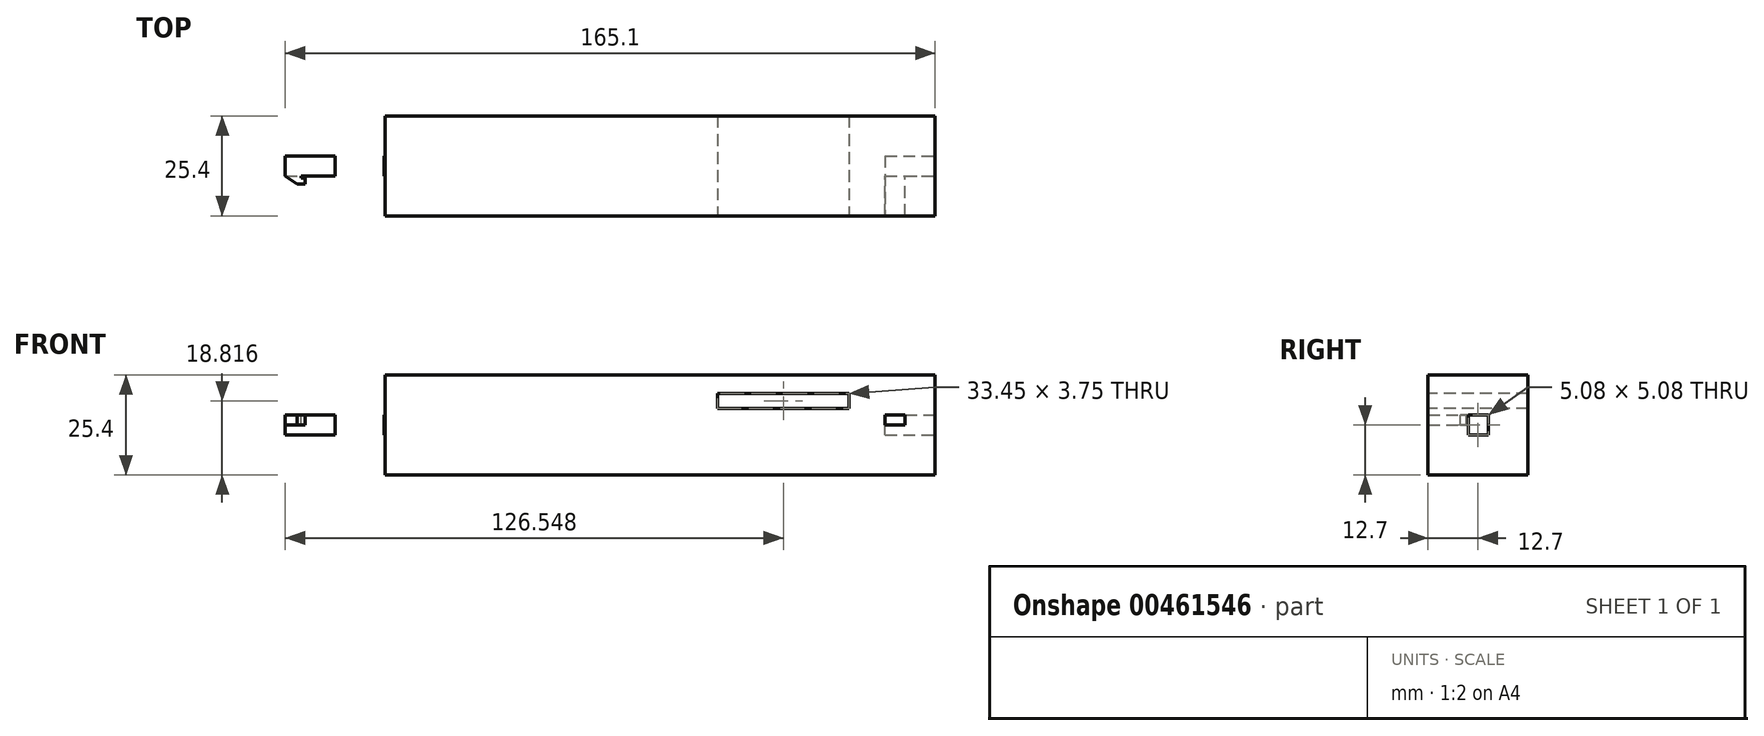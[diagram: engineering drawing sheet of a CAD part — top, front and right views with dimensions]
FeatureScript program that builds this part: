
annotation { "Feature Type Name" : "Feature", "Feature Type Description" : "" }
export const myFeature = defineFeature(function(context is Context, id is Id, definition is map)
    precondition{}
    {
        {
            var Q0;
            Q0=qCreatedBy(makeId("Top.planeOp"),FACE);
            var sketch = newSketch(context, id + "F0", { "sketchPlane" : qUnion([Q0])});
            skLineSegment(sketch, "E0.bottom", {"start": v(76.2, -12.7) * mm, "end": v(-76.2, -12.7) * mm});
            skLineSegment(sketch, "E0.top", {"start": v(76.2, 12.7) * mm, "end": v(-76.2, 12.7) * mm});
            skLineSegment(sketch, "E0.left", {"start": v(76.2, -12.7) * mm, "end": v(76.2, 12.7) * mm});
            skLineSegment(sketch, "E0.right", {"start": v(-76.2, -12.7) * mm, "end": v(-76.2, 12.7) * mm});
            skPoint(sketch, "E0.middle", {"position": v(0, 0) * mm});
            skSolve(sketch);
        }
        {
            var Q0;
            Q0 = qSketchRegion(id + "F0", true);
            var Q1;
            Q1=makeQuery(id+"F0.imprint","IMPRINT",FACE,{"disambiguationData":[TD([[makeQuery(id+"F0.imprint","IMPRINT",EDGE,{"derivedFrom":sQuery(id+"F0.wireOp",EDGE,"E0.bottom")}),-1.0]])]});
            extrude(context, id + "F1", {"entities" : qUnion([Q0, Q1]), "depth" : 25.4 * mm});
        }
        {
            var Q0;
            Q0=makeQuery(id+"F1.opExtrude","SWEPT_FACE",FACE,{"disambiguationData":[OSD([sQuery(id+"F0.wireOp",EDGE,"E0.left")])]});
            var sketch = newSketch(context, id + "F2", { "sketchPlane" : qUnion([Q0])});
            skLineSegment(sketch, "E1.bottom", {"start": v(2.54, 10.16) * mm, "end": v(-2.54, 10.16) * mm});
            skLineSegment(sketch, "E1.top", {"start": v(2.54, 15.24) * mm, "end": v(-2.54, 15.24) * mm});
            skLineSegment(sketch, "E1.left", {"start": v(2.54, 10.16) * mm, "end": v(2.54, 15.24) * mm});
            skLineSegment(sketch, "E1.right", {"start": v(-2.54, 10.16) * mm, "end": v(-2.54, 15.24) * mm});
            skPoint(sketch, "E1.middle", {"position": v(0, 12.7) * mm});
            skPoint(sketch, "E1.middle.positionSnap0", {"position": v(12.7, 12.7) * mm});
            skPoint(sketch, "E1.centerSnap0", {"position": v(12.7, 12.7) * mm});
            skSolve(sketch);
        }
        {
            var Q0;
            Q0 = qSketchRegion(id + "F2", true);
            extrude(context, id + "F3", {"entities" : qUnion([Q0]), "operationType" : NewBodyOperationType.REMOVE, "oppositeDirection" : true, "depth" : 12.7 * mm});
        }
        {
            var Q0;
            Q0=makeQuery(id+"F3.boolean.opBoolean","COPY",FACE,{"derivedFrom":makeQuery(id+"F3.opExtrude","SWEPT_FACE",FACE,{"disambiguationData":[OSD([sQuery(id+"F2.wireOp",EDGE,"E1.right")])]})});
            var sketch = newSketch(context, id + "F4", { "sketchPlane" : qUnion([Q0])});
            skLineSegment(sketch, "E2.bottom", {"start": v(-63.5, 15.24) * mm, "end": v(-68.58, 15.24) * mm});
            skLineSegment(sketch, "E2.top", {"start": v(-63.5, 12.7) * mm, "end": v(-68.58, 12.7) * mm});
            skLineSegment(sketch, "E2.left", {"start": v(-63.5, 15.24) * mm, "end": v(-63.5, 12.7) * mm});
            skLineSegment(sketch, "E2.right", {"start": v(-68.58, 15.24) * mm, "end": v(-68.58, 12.7) * mm});
            skSolve(sketch);
        }
        {
            var Q0;
            Q0=makeQuery(id+"F1.opExtrude","SWEPT_FACE",FACE,{"disambiguationData":[OSD([sQuery(id+"F0.wireOp",EDGE,"E0.right")])]});
            var sketch = newSketch(context, id + "F5", { "sketchPlane" : qUnion([Q0])});
            skLineSegment(sketch, "E3.bottom", {"start": v(2.54, 10.16) * mm, "end": v(-2.54, 10.16) * mm});
            skLineSegment(sketch, "E3.top", {"start": v(2.54, 15.24) * mm, "end": v(-2.54, 15.24) * mm});
            skLineSegment(sketch, "E3.left", {"start": v(2.54, 10.16) * mm, "end": v(2.54, 15.24) * mm});
            skLineSegment(sketch, "E3.right", {"start": v(-2.54, 10.16) * mm, "end": v(-2.54, 15.24) * mm});
            skPoint(sketch, "E3.middle", {"position": v(0, 12.7) * mm});
            skPoint(sketch, "E3.middle.positionSnap0", {"position": v(12.7, 12.7) * mm});
            skPoint(sketch, "E3.centerSnap0", {"position": v(12.7, 12.7) * mm});
            skSolve(sketch);
        }
        {
            var Q0;
            Q0 = qSketchRegion(id + "F5", true);
            extrude(context, id + "F6", {"entities" : qUnion([Q0]), "operationType" : NewBodyOperationType.ADD, "depth" : 12.7 * mm});
        }
        {
            var Q0;
            Q0=makeQuery(id+"F6.opExtrude","SWEPT_FACE",FACE,{"disambiguationData":[OSD([sQuery(id+"F5.wireOp",EDGE,"E3.top")])]});
            var sketch = newSketch(context, id + "F7", { "sketchPlane" : qUnion([Q0])});
            skLineSegment(sketch, "E4", {"start": v(-88.9, -2.54) * mm, "end": v(-83.83, -2.54) * mm});
            skLineSegment(sketch, "E5", {"start": v(-83.83, -2.54) * mm, "end": v(-83.83, -4.57) * mm});
            skLineSegment(sketch, "E6", {"start": v(-83.83, -4.57) * mm, "end": v(-85.86, -4.57) * mm});
            skLineSegment(sketch, "E7", {"start": v(-85.86, -4.57) * mm, "end": v(-88.9, -2.54) * mm});
            skSolve(sketch);
        }
        {
            var Q0;
            Q0=makeQuery(id+"F7.imprint","IMPRINT",FACE,{"disambiguationData":[TD([[makeQuery(id+"F7.imprint","IMPRINT",EDGE,{"derivedFrom":sQuery(id+"F7.wireOp",EDGE,"E4")}),-1.0]])]});
            extrude(context, id + "F8", {"entities" : qUnion([Q0]), "operationType" : NewBodyOperationType.ADD, "oppositeDirection" : true, "depth" : 2.54 * mm});
        }
        {
            var Q0;
            Q0=makeQuery(id+"F8.boolean.opBoolean","MERGE",FACE,{"derivedFrom":[makeQuery(id+"F6.opExtrude","SWEPT_FACE",FACE,{"disambiguationData":[OSD([sQuery(id+"F5.wireOp",EDGE,"E3.top")])]}),makeQuery(id+"F8.opExtrude","CAP_FACE",FACE,{"disambiguationData":[OSD([sQuery(id+"F7.wireOp",EDGE,"E4"),sQuery(id+"F7.wireOp",EDGE,"E5"),sQuery(id+"F7.wireOp",EDGE,"E6"),sQuery(id+"F7.wireOp",EDGE,"E7")])],"isStart":true})]});
            var sketch = newSketch(context, id + "F9", { "sketchPlane" : qUnion([Q0])});
            skLineSegment(sketch, "E8.bottom", {"start": v(-83.83, -2.54) * mm, "end": v(-84.84, -2.54) * mm});
            skLineSegment(sketch, "E8.top", {"start": v(-83.83, -3.05) * mm, "end": v(-84.84, -3.05) * mm});
            skLineSegment(sketch, "E8.left", {"start": v(-83.83, -2.54) * mm, "end": v(-83.83, -3.05) * mm});
            skLineSegment(sketch, "E8.right", {"start": v(-84.84, -2.54) * mm, "end": v(-84.84, -3.05) * mm});
            skSolve(sketch);
        }
        {
            var Q0;
            Q0=makeQuery(id+"F9.imprint","IMPRINT",FACE,{"disambiguationData":[TD([[makeQuery(id+"F9.imprint","IMPRINT",EDGE,{"derivedFrom":sQuery(id+"F9.wireOp",EDGE,"E8.bottom")}),1.0]])]});
            extrude(context, id + "F10", {"entities" : qUnion([Q0]), "operationType" : NewBodyOperationType.REMOVE, "oppositeDirection" : true, "depth" : 25.4 * mm});
        }
        {
            var Q0;
            Q0=makeQuery(id+"F4.imprint","IMPRINT",FACE,{"disambiguationData":[TD([[makeQuery(id+"F4.imprint","IMPRINT",EDGE,{"derivedFrom":sQuery(id+"F4.wireOp",EDGE,"E2.bottom")}),1.0]])]});
            extrude(context, id + "F11", {"entities" : qUnion([Q0]), "operationType" : NewBodyOperationType.REMOVE, "oppositeDirection" : true, "depth" : 25.4 * mm});
        }
        {
            var Q0;
            Q0=makeQuery(id+"F1.opExtrude","SWEPT_FACE",FACE,{"disambiguationData":[OSD([sQuery(id+"F0.wireOp",EDGE,"E0.bottom")])]});
            var sketch = newSketch(context, id + "F12", { "sketchPlane" : qUnion([Q0])});
            skLineSegment(sketch, "E9.bottom", {"start": v(20.92, 20.7) * mm, "end": v(54.37, 20.7) * mm});
            skLineSegment(sketch, "E9.top", {"start": v(20.92, 16.94) * mm, "end": v(54.37, 16.94) * mm});
            skLineSegment(sketch, "E9.left", {"start": v(20.92, 20.7) * mm, "end": v(20.92, 16.94) * mm});
            skLineSegment(sketch, "E9.right", {"start": v(54.37, 20.7) * mm, "end": v(54.37, 16.94) * mm});
            skSolve(sketch);
        }
        {
            var Q0;
            Q0=makeQuery(id+"F12.imprint","IMPRINT",FACE,{"disambiguationData":[TD([[makeQuery(id+"F12.imprint","IMPRINT",EDGE,{"derivedFrom":sQuery(id+"F12.wireOp",EDGE,"E9.bottom")}),-1.0]])]});
            extrude(context, id + "F13", {"entities" : qUnion([Q0]), "operationType" : NewBodyOperationType.REMOVE, "oppositeDirection" : true, "depth" : 25.4 * mm});
        }
        {
            var Q0;
            Q0=makeQuery(id+"F1.opExtrude","CAP_FACE",FACE,{"disambiguationData":[OSD([sQuery(id+"F0.wireOp",EDGE,"E0.bottom"),sQuery(id+"F0.wireOp",EDGE,"E0.top"),sQuery(id+"F0.wireOp",EDGE,"E0.left"),sQuery(id+"F0.wireOp",EDGE,"E0.right")])],"isStart":false});
            var sketch = newSketch(context, id + "F14", { "sketchPlane" : qUnion([Q0])});
            skLineSegment(sketch, "E10.bottom", {"start": v(-76.2, 12.7) * mm, "end": v(-63.5, 12.7) * mm});
            skLineSegment(sketch, "E10.top", {"start": v(-76.2, -12.7) * mm, "end": v(-63.5, -12.7) * mm});
            skLineSegment(sketch, "E10.left", {"start": v(-76.2, 12.7) * mm, "end": v(-76.2, -12.7) * mm});
            skLineSegment(sketch, "E10.right", {"start": v(-63.5, 12.7) * mm, "end": v(-63.5, -12.7) * mm});
            skSolve(sketch);
        }
        {
            var Q0;
            Q0=makeQuery(id+"F14.imprint","IMPRINT",FACE,{"disambiguationData":[TD([[makeQuery(id+"F14.imprint","IMPRINT",EDGE,{"derivedFrom":sQuery(id+"F14.wireOp",EDGE,"E10.bottom")}),1.0]])]});
            extrude(context, id + "F15", {"entities" : qUnion([Q0]), "operationType" : NewBodyOperationType.REMOVE, "oppositeDirection" : true, "depth" : 25.4 * mm});
        }
        {
            var Q0;
            Q0=makeQuery(id+"F15.boolean.opBoolean","COPY",FACE,{"derivedFrom":makeQuery(id+"F15.opExtrude","SWEPT_FACE",FACE,{"disambiguationData":[OSD([sQuery(id+"F14.wireOp",EDGE,"E10.right")])]})});
            var sketch = newSketch(context, id + "F16", { "sketchPlane" : qUnion([Q0])});
            skLineSegment(sketch, "E11.bottom", {"start": v(2.54, 15.24) * mm, "end": v(-2.54, 15.24) * mm});
            skLineSegment(sketch, "E11.top", {"start": v(2.54, 10.16) * mm, "end": v(-2.54, 10.16) * mm});
            skLineSegment(sketch, "E11.left", {"start": v(2.54, 15.24) * mm, "end": v(2.54, 10.16) * mm});
            skLineSegment(sketch, "E11.right", {"start": v(-2.54, 15.24) * mm, "end": v(-2.54, 10.16) * mm});
            skPoint(sketch, "E11.middle", {"position": v(0, 12.7) * mm});
            skSolve(sketch);
        }
        {
            var Q0;
            Q0=makeQuery(id+"F16.imprint","IMPRINT",FACE,{"disambiguationData":[TD([[makeQuery(id+"F16.imprint","IMPRINT",EDGE,{"derivedFrom":sQuery(id+"F16.wireOp",EDGE,"E11.bottom")}),1.0]])]});
            extrude(context, id + "F17", {"entities" : qUnion([Q0]), "operationType" : NewBodyOperationType.ADD, "depth" : 0.25 * mm});
        }
    });
